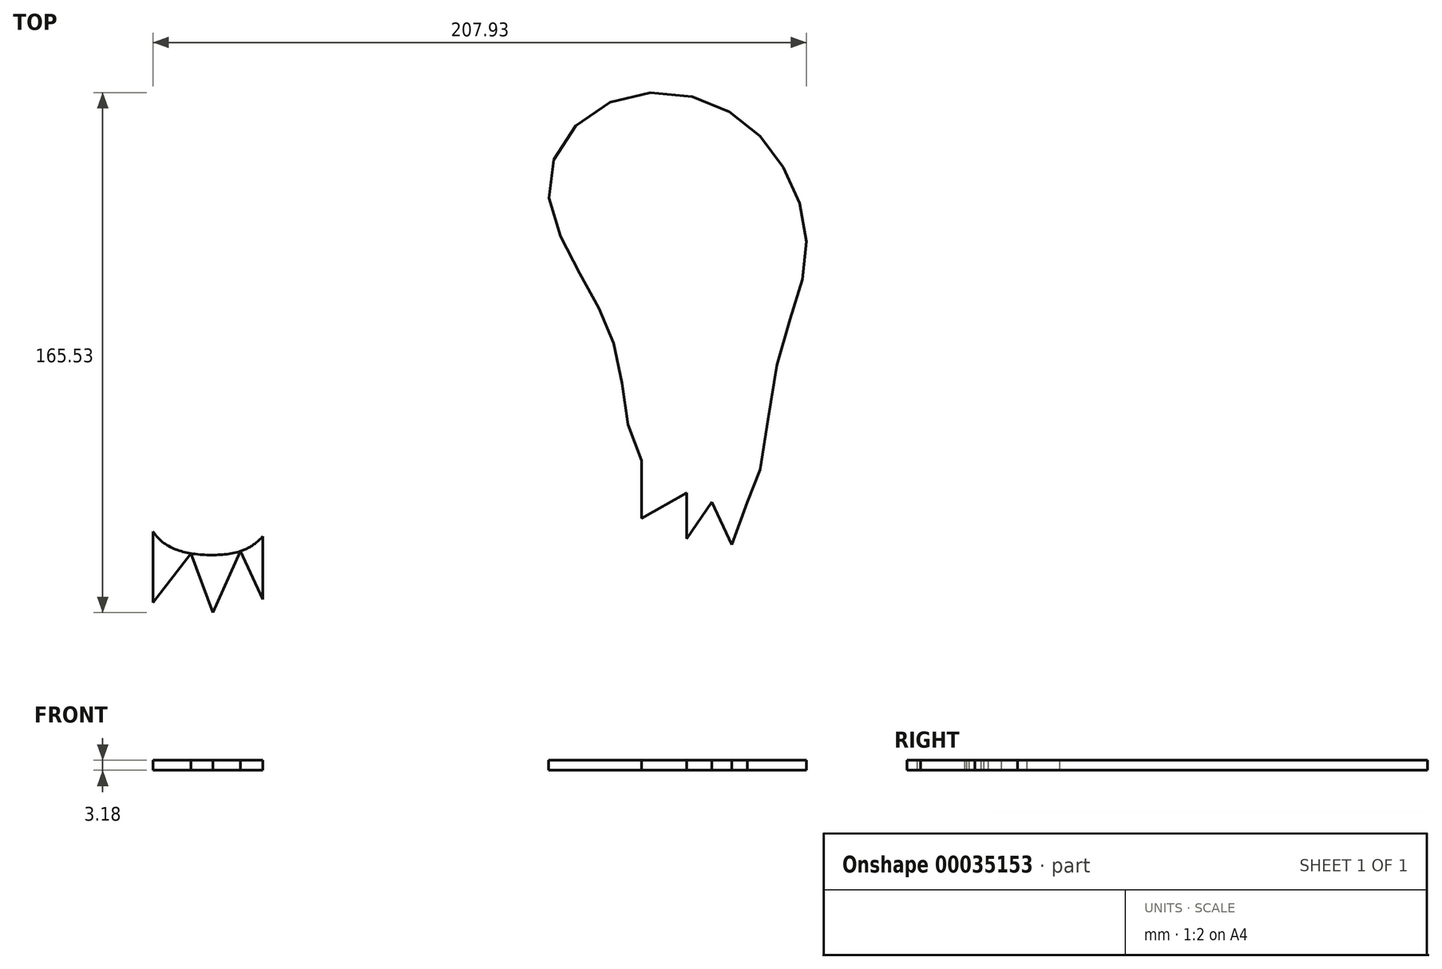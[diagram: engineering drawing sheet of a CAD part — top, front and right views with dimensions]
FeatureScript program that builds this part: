
annotation { "Feature Type Name" : "Feature", "Feature Type Description" : "" }
export const myFeature = defineFeature(function(context is Context, id is Id, definition is map)
    precondition{}
    {
        {
            var Q0;
            Q0=qCreatedBy(makeId("Top.planeOp"),FACE);
            var sketch = newSketch(context, id + "F0", { "sketchPlane" : qUnion([Q0])});
            skFitSpline(sketch, "E0", {"points": [v(-81.45, 79.6) * mm, v(-99.12, 79.6) * mm, v(-115.08, 63.36) * mm, v(-125.71, 25.33) * mm, v(-122.98, -8.17) * mm, v(-108.6, -28.2) * mm, v(-100.47, -65.38) * mm, v(-81.45, -72.8) * mm, v(-65.58, -66.84) * mm, v(-51.25, -26.56) * mm, v(-39.22, 21.29) * mm, v(-45.79, 62.92) * mm, v(-81.45, 79.6) * mm]});
            skFitSpline(sketch, "E1", {"points": [v(77.3, 71.03) * mm, v(99.6, 51.4) * mm, v(107.37, 22.75) * mm, v(97.8, -13.55) * mm, v(88.64, -55.97) * mm, v(77.3, -55.97) * mm, v(54.97, -42.75) * mm, v(47.52, -11.05) * mm, v(35.5, 16.5) * mm, v(25.47, 46.85) * mm, v(44.22, 71.03) * mm, v(77.3, 71.03) * mm]});
            skLineSegment(sketch, "E2", {"start": v(-100.47, -65.38) * mm, "end": v(-100.47, -88) * mm});
            skLineSegment(sketch, "E3", {"start": v(-100.47, -88) * mm, "end": v(-88.45, -72.3) * mm});
            skLineSegment(sketch, "E4", {"start": v(-88.45, -72.3) * mm, "end": v(-81.45, -91.16) * mm});
            skLineSegment(sketch, "E5", {"start": v(-81.45, -91.16) * mm, "end": v(-72.64, -71.59) * mm});
            skLineSegment(sketch, "E6", {"start": v(-72.64, -71.59) * mm, "end": v(-65.58, -86.88) * mm});
            skLineSegment(sketch, "E7", {"start": v(-65.58, -86.88) * mm, "end": v(-65.58, -66.84) * mm});
            skLineSegment(sketch, "E8", {"start": v(54.97, -42.75) * mm, "end": v(54.97, -61.2) * mm});
            skLineSegment(sketch, "E9", {"start": v(54.97, -61.2) * mm, "end": v(69.35, -53.07) * mm});
            skLineSegment(sketch, "E10", {"start": v(69.35, -53.07) * mm, "end": v(69.35, -67.66) * mm});
            skLineSegment(sketch, "E11", {"start": v(69.35, -67.66) * mm, "end": v(77.3, -55.97) * mm});
            skLineSegment(sketch, "E12", {"start": v(77.3, -55.97) * mm, "end": v(83.6, -69.57) * mm});
            skLineSegment(sketch, "E13", {"start": v(83.6, -69.57) * mm, "end": v(88.64, -55.97) * mm});
            skSolve(sketch);
        }
        {
            var Q0;
            {var subQ1=sQuery(id+"F0.wireOp",EDGE,"E12");Q0=makeQuery(id+"F0.imprint","IMPRINT",FACE,{"disambiguationData":[TD([[makeQuery(id+"F0.imprint","IMPRINT",EDGE,{"derivedFrom":subQ1}),1.0]])]});}
            var Q1;
            {var subQ1=sQuery(id+"F0.wireOp",EDGE,"115aa28d-62a3-4706-a7cf-55b58465c164");var subQ3=sQuery(id+"F0.wireOp",EDGE,"E1");var subQ5=makeQuery(id+"F0.imprint","INTERSECT",VERTEX,{"derivedFrom":[subQ1,subQ3]});Q1=makeQuery(id+"F0.imprint","IMPRINT",FACE,{"disambiguationData":[TD([[makeQuery(id+"F0.imprint","IMPRINT",EDGE,{"disambiguationData":[TD([[subQ5,-1.0]])],"derivedFrom":subQ1}),1.0]])]});}
            var Q2;
            {var subQ1=sQuery(id+"F0.wireOp",EDGE,"115aa28d-62a3-4706-a7cf-55b58465c164");var subQ3=sQuery(id+"F0.wireOp",EDGE,"E1");var subQ5=makeQuery(id+"F0.imprint","INTERSECT",VERTEX,{"derivedFrom":[subQ1,subQ3]});Q2=makeQuery(id+"F0.imprint","IMPRINT",FACE,{"disambiguationData":[TD([[makeQuery(id+"F0.imprint","IMPRINT",EDGE,{"disambiguationData":[TD([[subQ5,-1.0]])],"derivedFrom":subQ1}),-1.0]])]});}
            var Q3;
            {var subQ1=sQuery(id+"F0.wireOp",EDGE,"E8");Q3=makeQuery(id+"F0.imprint","IMPRINT",FACE,{"disambiguationData":[TD([[makeQuery(id+"F0.imprint","IMPRINT",EDGE,{"derivedFrom":subQ1}),1.0]])]});}
            var Q4;
            {var subQ1=sQuery(id+"F0.wireOp",EDGE,"8a344740-1494-4c66-a654-d00c580876b4");var subQ5=sQuery(id+"F0.wireOp",EDGE,"b921b1f0-fb51-44a1-9a93-3b7e9cbc0e22");var subQ6=makeQuery(id+"F0.imprint","INTERSECT",VERTEX,{"derivedFrom":[subQ1,subQ5]});Q4=makeQuery(id+"F0.imprint","IMPRINT",FACE,{"disambiguationData":[TD([[makeQuery(id+"F0.imprint","IMPRINT",EDGE,{"disambiguationData":[TD([[subQ6,-1.0]])],"derivedFrom":subQ1}),-1.0]])]});}
            var Q5;
            {var subQ3=sQuery(id+"F0.wireOp",EDGE,"E1");var subQ5=makeQuery(id+"F0.imprint","INTERSECT",VERTEX,{"derivedFrom":[subQ3,sQuery(id+"F0.wireOp",EDGE,"E13")]});Q5=makeQuery(id+"F0.imprint","IMPRINT",FACE,{"disambiguationData":[TD([[makeQuery(id+"F0.imprint","IMPRINT",EDGE,{"disambiguationData":[TD([[subQ5,1.0]])],"derivedFrom":subQ3}),-1.0]])]});}
            var Q6;
            {var subQ1=sQuery(id+"F0.wireOp",EDGE,"E10");Q6=makeQuery(id+"F0.imprint","IMPRINT",FACE,{"disambiguationData":[TD([[makeQuery(id+"F0.imprint","IMPRINT",EDGE,{"derivedFrom":subQ1}),1.0]])]});}
            var Q7;
            {var subQ1=sQuery(id+"F0.wireOp",EDGE,"8a344740-1494-4c66-a654-d00c580876b4");var subQ3=sQuery(id+"F0.wireOp",EDGE,"E0");var subQ5=makeQuery(id+"F0.imprint","INTERSECT",VERTEX,{"disambiguationData":[OD(0.0)],"derivedFrom":[subQ1,subQ3]});Q7=makeQuery(id+"F0.imprint","IMPRINT",FACE,{"disambiguationData":[TD([[makeQuery(id+"F0.imprint","IMPRINT",EDGE,{"disambiguationData":[TD([[subQ5,-1.0]])],"derivedFrom":subQ1}),-1.0]])]});}
            var Q8;
            {var subQ1=sQuery(id+"F0.wireOp",EDGE,"8a344740-1494-4c66-a654-d00c580876b4");var subQ3=sQuery(id+"F0.wireOp",EDGE,"E0");var subQ6=makeQuery(id+"F0.imprint","INTERSECT",VERTEX,{"disambiguationData":[OD(1.0)],"derivedFrom":[subQ1,subQ3]});Q8=makeQuery(id+"F0.imprint","IMPRINT",FACE,{"disambiguationData":[TD([[makeQuery(id+"F0.imprint","IMPRINT",EDGE,{"disambiguationData":[TD([[subQ6,1.0]])],"derivedFrom":subQ1}),-1.0]])]});}
            var Q9;
            {var subQ1=sQuery(id+"F0.wireOp",EDGE,"8a344740-1494-4c66-a654-d00c580876b4");var subQ3=sQuery(id+"F0.wireOp",EDGE,"E0");var subQ7=makeQuery(id+"F0.imprint","INTERSECT",VERTEX,{"disambiguationData":[OD(1.0)],"derivedFrom":[subQ1,subQ3]});Q9=makeQuery(id+"F0.imprint","IMPRINT",FACE,{"disambiguationData":[TD([[makeQuery(id+"F0.imprint","IMPRINT",EDGE,{"disambiguationData":[TD([[subQ7,1.0]])],"derivedFrom":subQ1}),1.0]])]});}
            var Q10;
            {var subQ1=sQuery(id+"F0.wireOp",EDGE,"8a344740-1494-4c66-a654-d00c580876b4");var subQ5=sQuery(id+"F0.wireOp",EDGE,"b921b1f0-fb51-44a1-9a93-3b7e9cbc0e22");var subQ6=makeQuery(id+"F0.imprint","INTERSECT",VERTEX,{"derivedFrom":[subQ1,subQ5]});Q10=makeQuery(id+"F0.imprint","IMPRINT",FACE,{"disambiguationData":[TD([[makeQuery(id+"F0.imprint","IMPRINT",EDGE,{"disambiguationData":[TD([[subQ6,-1.0]])],"derivedFrom":subQ1}),1.0]])]});}
            var Q11;
            {var subQ1=sQuery(id+"F0.wireOp",EDGE,"E4");Q11=makeQuery(id+"F0.imprint","IMPRINT",FACE,{"disambiguationData":[TD([[makeQuery(id+"F0.imprint","IMPRINT",EDGE,{"derivedFrom":subQ1}),1.0]])]});}
            var Q12;
            {var subQ1=sQuery(id+"F0.wireOp",EDGE,"E2");Q12=makeQuery(id+"F0.imprint","IMPRINT",FACE,{"disambiguationData":[TD([[makeQuery(id+"F0.imprint","IMPRINT",EDGE,{"derivedFrom":subQ1}),1.0]])]});}
            var Q13;
            {var subQ0=sQuery(id+"F0.wireOp",EDGE,"E6");Q13=makeQuery(id+"F0.imprint","IMPRINT",FACE,{"disambiguationData":[TD([[makeQuery(id+"F0.imprint","IMPRINT",EDGE,{"derivedFrom":subQ0}),1.0]])]});}
            var Q14;
            {var subQ1=sQuery(id+"F0.wireOp",EDGE,"8a344740-1494-4c66-a654-d00c580876b4");var subQ3=sQuery(id+"F0.wireOp",EDGE,"E0");var subQ5=makeQuery(id+"F0.imprint","INTERSECT",VERTEX,{"disambiguationData":[OD(0.0)],"derivedFrom":[subQ1,subQ3]});Q14=makeQuery(id+"F0.imprint","IMPRINT",FACE,{"disambiguationData":[TD([[makeQuery(id+"F0.imprint","IMPRINT",EDGE,{"disambiguationData":[TD([[subQ5,-1.0]])],"derivedFrom":subQ1}),1.0]])]});}
            var Q15;
            {var subQ3=sQuery(id+"F0.wireOp",EDGE,"E1");var subQ5=makeQuery(id+"F0.imprint","INTERSECT",VERTEX,{"derivedFrom":[subQ3,sQuery(id+"F0.wireOp",EDGE,"E8")]});Q15=makeQuery(id+"F0.imprint","IMPRINT",FACE,{"disambiguationData":[TD([[makeQuery(id+"F0.imprint","IMPRINT",EDGE,{"disambiguationData":[TD([[subQ5,-1.0]])],"derivedFrom":subQ3}),-1.0]])]});}
            extrude(context, id + "F1", {"entities" : qUnion([Q0, Q1, Q2, Q3, Q4, Q5, Q6, Q7, Q8, Q9, Q10, Q11, Q12, Q13, Q14, Q15]), "depth" : 3.17 * mm});
        }
    });
